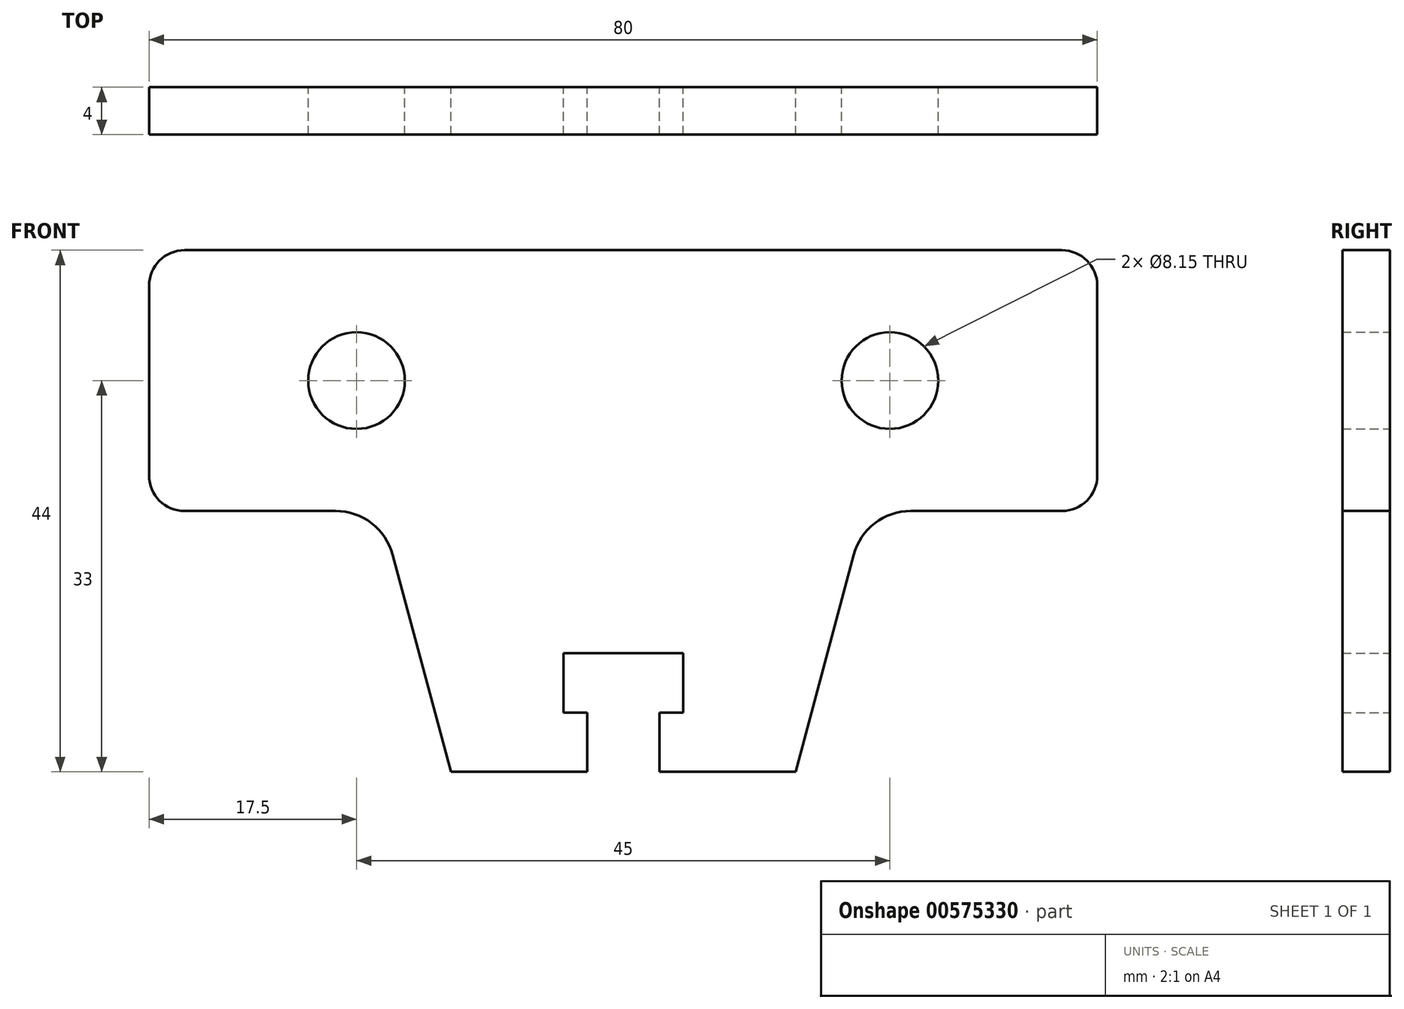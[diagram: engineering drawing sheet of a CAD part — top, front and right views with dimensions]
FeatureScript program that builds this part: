
annotation { "Feature Type Name" : "Feature", "Feature Type Description" : "" }
export const myFeature = defineFeature(function(context is Context, id is Id, definition is map)
    precondition{}
    {
        {
            var Q0;
            Q0=qCreatedBy(makeId("Front.planeOp"),FACE);
            var sketch = newSketch(context, id + "F0", { "sketchPlane" : qUnion([Q0])});
            skLineSegment(sketch, "E0", {"start": v(0, 0) * mm, "end": v(-37, 0) * mm});
            skLineSegment(sketch, "E1", {"start": v(-40, -3) * mm, "end": v(-40, -19) * mm});
            skLineSegment(sketch, "E2", {"start": v(-37, -22) * mm, "end": v(-24.27, -22) * mm});
            skLineSegment(sketch, "E3", {"start": v(-19.44, -25.7) * mm, "end": v(-14.54, -44) * mm});
            skLineSegment(sketch, "E4", {"start": v(-14.54, -44) * mm, "end": v(-3.05, -44) * mm});
            skLineSegment(sketch, "E5", {"start": v(-3.05, -44) * mm, "end": v(-3.05, -39) * mm});
            skLineSegment(sketch, "E6", {"start": v(-3.05, -39) * mm, "end": v(-5.05, -39) * mm});
            skLineSegment(sketch, "E7", {"start": v(-5.05, -39) * mm, "end": v(-5.05, -34) * mm});
            skLineSegment(sketch, "E8", {"start": v(-5.05, -34) * mm, "end": v(0, -34) * mm});
            skLineSegment(sketch, "E9", {"start": v(0, -34) * mm, "end": v(0, 0) * mm});
            skCircle(sketch, "E10", {"center": v(-22.5, -11) * mm, "radius": 4.08 * mm});
            skPoint(sketch, "E11.visualSharp", {"position": v(-20.43, -22) * mm});
            skArc(sketch, "E11.filletArc", {"start": v(-19.44, -25.7) * mm, "mid": v(-21.23, -23.03) * mm, "end": v(-24.27, -22) * mm});
            skPoint(sketch, "E12.visualSharp", {"position": v(-40, 0) * mm});
            skArc(sketch, "E12.filletArc", {"start": v(-37, 0) * mm, "mid": v(-39.12, -0.88) * mm, "end": v(-40, -3) * mm});
            skPoint(sketch, "E13.visualSharp", {"position": v(-40, -22) * mm});
            skArc(sketch, "E13.filletArc", {"start": v(-40, -19) * mm, "mid": v(-39.12, -21.12) * mm, "end": v(-37, -22) * mm});
            skSolve(sketch);
        }
        {
            var Q0;
            Q0=makeQuery(id+"F0.imprint","IMPRINT",FACE,{"disambiguationData":[TD([[makeQuery(id+"F0.imprint","IMPRINT",EDGE,{"derivedFrom":sQuery(id+"F0.wireOp",EDGE,"E0")}),1.0]])]});
            extrude(context, id + "F1", {"entities" : qUnion([Q0]), "depth" : 4 * mm, "offsetDistance" : 25 * mm});
        }
        {
            var Q0;
            Q0=makeQuery(id+"F1.opExtrude","SWEPT_BODY",BODY,{"disambiguationData":[OSD([sQuery(id+"F0.wireOp",EDGE,"E0"),sQuery(id+"F0.wireOp",EDGE,"E1"),sQuery(id+"F0.wireOp",EDGE,"E2"),sQuery(id+"F0.wireOp",EDGE,"E3"),sQuery(id+"F0.wireOp",EDGE,"E4"),sQuery(id+"F0.wireOp",EDGE,"E5"),sQuery(id+"F0.wireOp",EDGE,"E6"),sQuery(id+"F0.wireOp",EDGE,"E7"),sQuery(id+"F0.wireOp",EDGE,"E8"),sQuery(id+"F0.wireOp",EDGE,"E9"),sQuery(id+"F0.wireOp",EDGE,"E10"),sQuery(id+"F0.wireOp",EDGE,"E11.filletArc"),sQuery(id+"F0.wireOp",EDGE,"E12.filletArc"),sQuery(id+"F0.wireOp",EDGE,"E13.filletArc")])]});
            var Q1;
            Q1=makeQuery(id+"F1.opExtrude","SWEPT_FACE",FACE,{"disambiguationData":[OSD([sQuery(id+"F0.wireOp",EDGE,"E9")])]});
            mirror(context, id + "F2", {"operationType" : NewBodyOperationType.ADD, "entities" : qUnion([Q0]), "mirrorPlane" : qUnion([Q1])});
        }
    });
